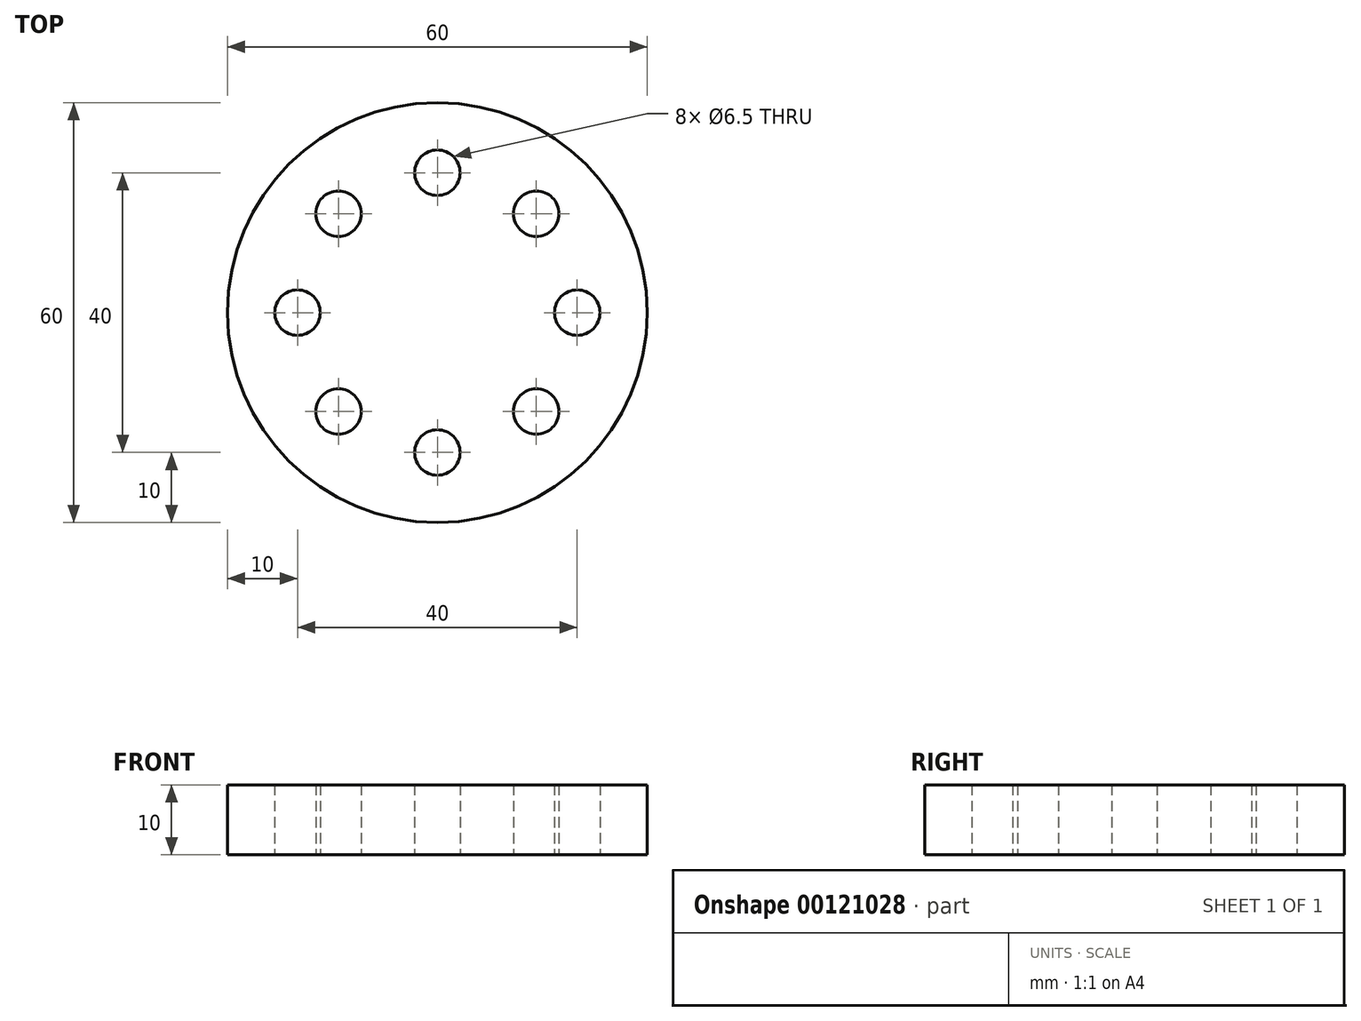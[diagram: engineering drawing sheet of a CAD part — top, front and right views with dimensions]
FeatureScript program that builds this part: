
annotation { "Feature Type Name" : "Feature", "Feature Type Description" : "" }
export const myFeature = defineFeature(function(context is Context, id is Id, definition is map)
    precondition{}
    {
        {
            var Q0;
            Q0=qCreatedBy(makeId("Top.planeOp"),FACE);
            var sketch = newSketch(context, id + "F0", { "sketchPlane" : qUnion([Q0])});
            skCircle(sketch, "E0", {"center": v(0, 0) * mm, "radius": 30 * mm});
            skCircle(sketch, "E1", {"center": v(0, 20) * mm, "radius": 3.25 * mm});
            skCircle(sketch, "E2.1.0", {"center": v(-14.14, 14.14) * mm, "radius": 3.25 * mm});
            skCircle(sketch, "E2.2.0", {"center": v(-20, 0) * mm, "radius": 3.25 * mm});
            skCircle(sketch, "E3.1.3.0", {"center": v(-14.14, -14.14) * mm, "radius": 3.25 * mm});
            skCircle(sketch, "E3.1.4.0", {"center": v(0, -20) * mm, "radius": 3.25 * mm});
            skCircle(sketch, "E3.1.5.0", {"center": v(14.14, -14.14) * mm, "radius": 3.25 * mm});
            skCircle(sketch, "E3.1.6.0", {"center": v(20, 0) * mm, "radius": 3.25 * mm});
            skCircle(sketch, "E3.1.7.0", {"center": v(14.14, 14.14) * mm, "radius": 3.25 * mm});
            skSolve(sketch);
        }
        {
            var Q0;
            Q0=makeQuery(id+"F0.imprint","IMPRINT",FACE,{"disambiguationData":[TD([[makeQuery(id+"F0.imprint","IMPRINT",EDGE,{"derivedFrom":sQuery(id+"F0.wireOp",EDGE,"E0")}),1.0]])]});
            extrude(context, id + "F1", {"entities" : qUnion([Q0]), "depth" : 10 * mm});
        }
    });
